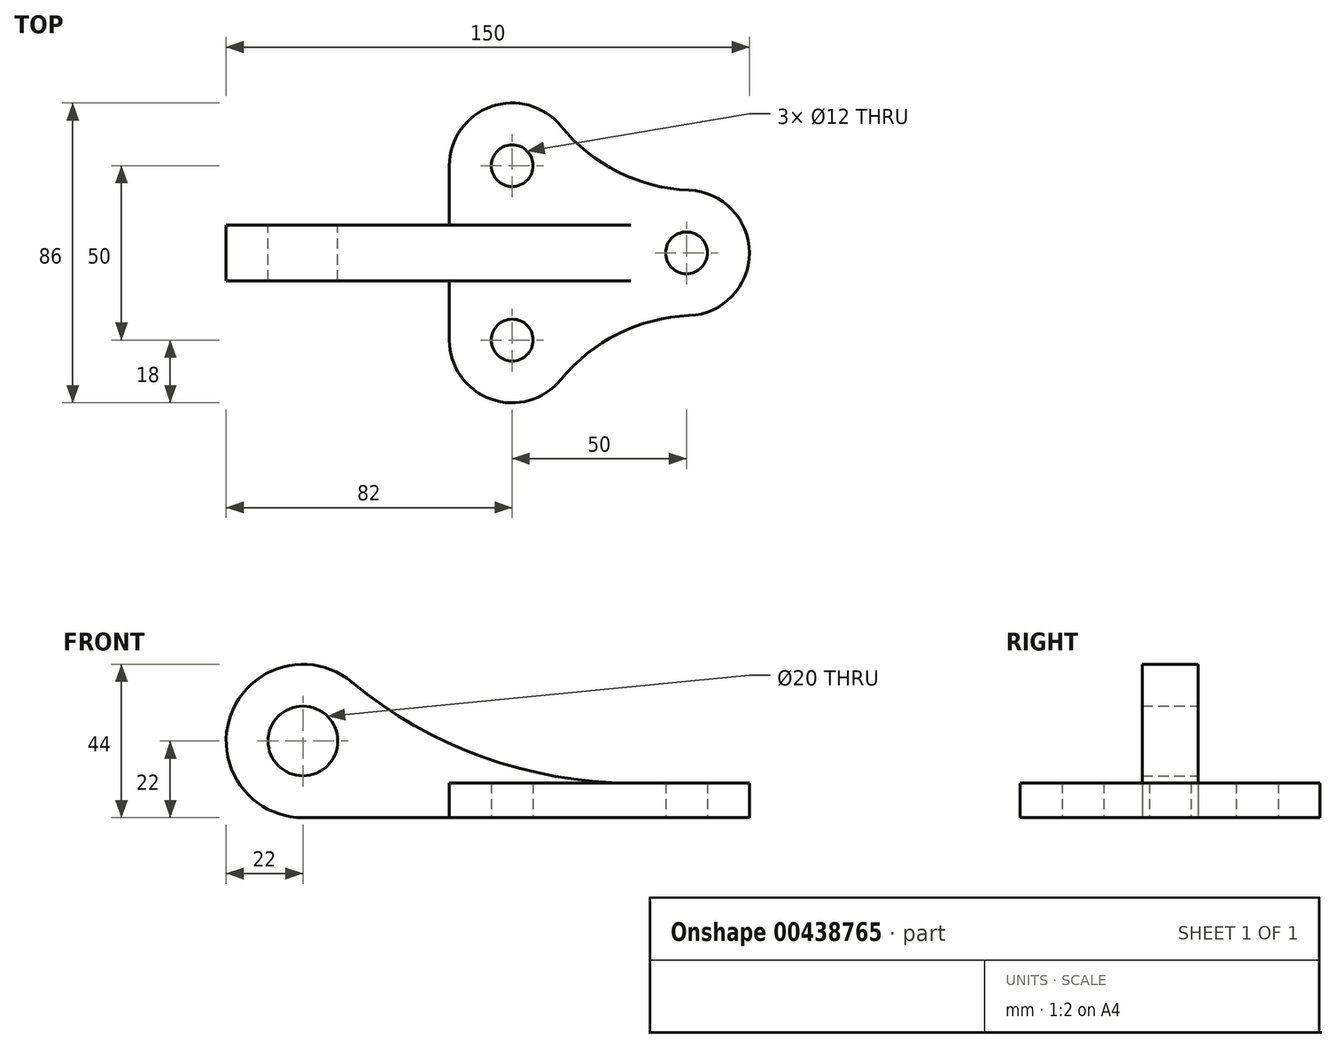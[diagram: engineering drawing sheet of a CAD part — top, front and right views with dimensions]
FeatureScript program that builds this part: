
annotation { "Feature Type Name" : "Feature", "Feature Type Description" : "" }
export const myFeature = defineFeature(function(context is Context, id is Id, definition is map)
    precondition{}
    {
        {
            var Q0;
            Q0=qCreatedBy(makeId("Top.planeOp"),FACE);
            var sketch = newSketch(context, id + "F0", { "sketchPlane" : qUnion([Q0])});
            skCircle(sketch, "E0", {"center": v(50, 0) * mm, "radius": 6 * mm});
            skCircle(sketch, "E1", {"center": v(0, 25) * mm, "radius": 6 * mm});
            skCircle(sketch, "E2", {"center": v(0, -25) * mm, "radius": 6 * mm});
            skArc(sketch, "E3", {"start": v(50.72, 17.99) * mm, "mid": v(68, 0) * mm, "end": v(50.72, -17.99) * mm});
            skArc(sketch, "E4", {"start": v(-18, -25) * mm, "mid": v(-6.03, -41.96) * mm, "end": v(13.96, -36.37) * mm});
            skArc(sketch, "E5", {"start": v(-18, 25) * mm, "mid": v(-6.03, 41.96) * mm, "end": v(13.96, 36.37) * mm});
            skArc(sketch, "E6", {"start": v(13.96, 36.37) * mm, "mid": v(30.36, 23.22) * mm, "end": v(50.72, 17.99) * mm});
            skArc(sketch, "E7", {"start": v(50.72, -17.99) * mm, "mid": v(30.36, -23.22) * mm, "end": v(13.96, -36.37) * mm});
            skLineSegment(sketch, "E8", {"start": v(-18, 25) * mm, "end": v(-18, -25) * mm});
            skSolve(sketch);
        }
        {
            var Q0;
            Q0=makeQuery(id+"F0.imprint","IMPRINT",FACE,{"disambiguationData":[TD([[makeQuery(id+"F0.imprint","IMPRINT",EDGE,{"derivedFrom":sQuery(id+"F0.wireOp",EDGE,"E0")}),-1.0]])]});
            extrude(context, id + "F1", {"entities" : qUnion([Q0]), "depth" : 10 * mm});
        }
        {
            var Q0;
            Q0=qCreatedBy(makeId("Front.planeOp"),FACE);
            var sketch = newSketch(context, id + "F2", { "sketchPlane" : qUnion([Q0])});
            skCircle(sketch, "E9", {"center": v(-60, 22) * mm, "radius": 10 * mm});
            skArc(sketch, "E10", {"start": v(-60, 0) * mm, "mid": v(-80.69, 29.48) * mm, "end": v(-45.93, 38.91) * mm});
            skLineSegment(sketch, "E11", {"start": v(-60, 0) * mm, "end": v(50, 0) * mm});
            skArc(sketch, "E12", {"start": v(-45.93, 38.91) * mm, "mid": v(-8.49, 17.45) * mm, "end": v(34.02, 10) * mm});
            skLineSegment(sketch, "E13", {"start": v(34.02, 10) * mm, "end": v(34.02, 0) * mm});
            skSolve(sketch);
        }
        {
            var Q0;
            Q0=makeQuery(id+"F2.imprint","IMPRINT",FACE,{"disambiguationData":[TD([[makeQuery(id+"F2.imprint","IMPRINT",EDGE,{"derivedFrom":sQuery(id+"F2.wireOp",EDGE,"E9")}),-1.0]])]});
            extrude(context, id + "F3", {"entities" : qUnion([Q0]), "operationType" : NewBodyOperationType.ADD, "depth" : 8 * mm});
        }
        {
            var Q0;
            Q0=makeQuery(id+"F2.imprint","IMPRINT",FACE,{"disambiguationData":[TD([[makeQuery(id+"F2.imprint","IMPRINT",EDGE,{"derivedFrom":sQuery(id+"F2.wireOp",EDGE,"E9")}),-1.0]])]});
            extrude(context, id + "F4", {"entities" : qUnion([Q0]), "operationType" : NewBodyOperationType.ADD, "oppositeDirection" : true, "depth" : 8 * mm});
        }
    });
